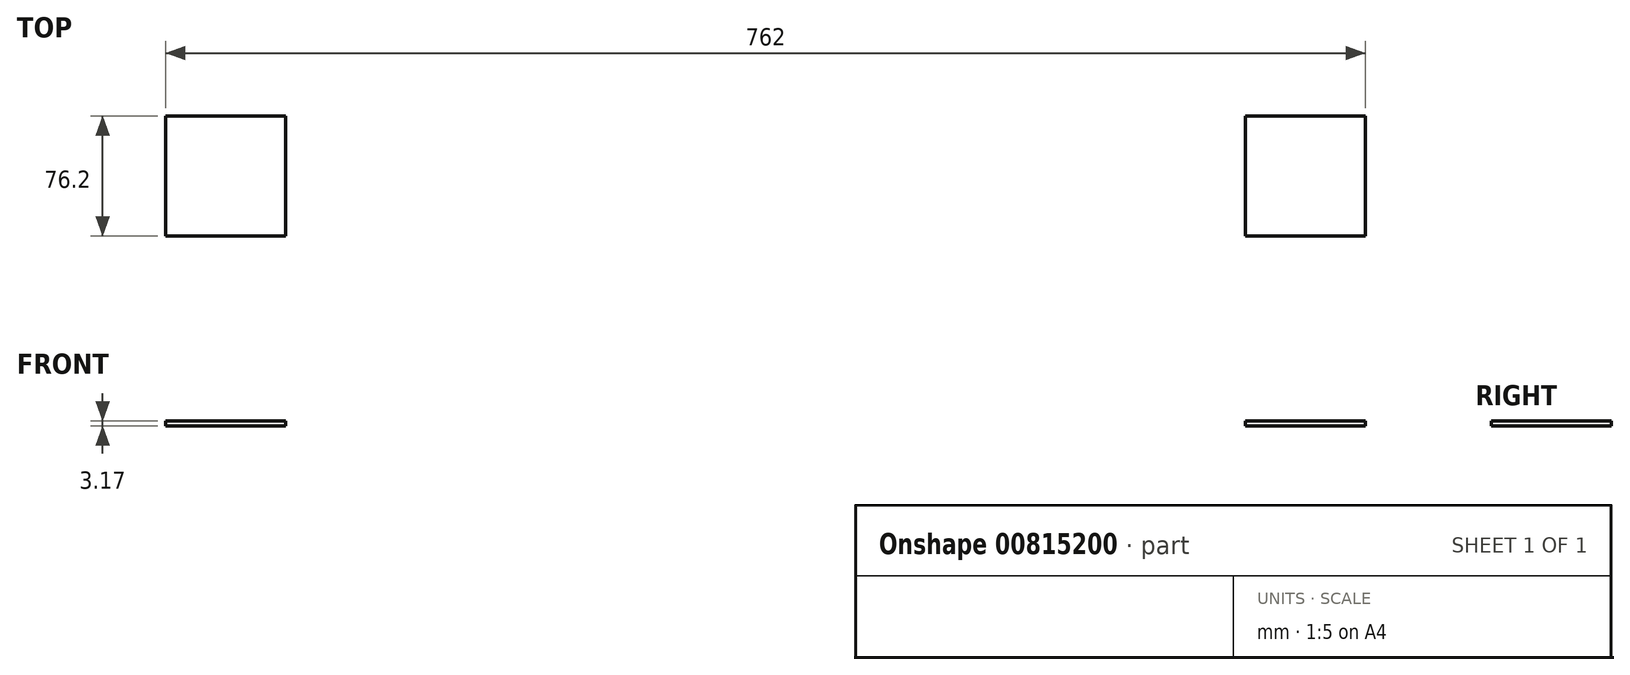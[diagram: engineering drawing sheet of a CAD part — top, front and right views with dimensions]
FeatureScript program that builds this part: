
annotation { "Feature Type Name" : "Feature", "Feature Type Description" : "" }
export const myFeature = defineFeature(function(context is Context, id is Id, definition is map)
    precondition{}
    {
        {
            var Q0;
            Q0=qCreatedBy(makeId("Top.planeOp"),FACE);
            var sketch = newSketch(context, id + "F0", { "sketchPlane" : qUnion([Q0])});
            skLineSegment(sketch, "E0.bottom", {"start": v(0, 0) * mm, "end": v(-762, 0) * mm});
            skLineSegment(sketch, "E0.top", {"start": v(0, -508) * mm, "end": v(-762, -508) * mm});
            skLineSegment(sketch, "E0.left", {"start": v(0, 0) * mm, "end": v(0, -508) * mm});
            skLineSegment(sketch, "E0.right", {"start": v(-762, 0) * mm, "end": v(-762, -508) * mm});
            skCircle(sketch, "E1", {"center": v(-101.6, -469.9) * mm, "radius": 12.7 * mm});
            skCircle(sketch, "E2.0.1.0", {"center": v(-101.6, -431.8) * mm, "radius": 12.7 * mm});
            skCircle(sketch, "E2.0.2.0", {"center": v(-101.6, -393.7) * mm, "radius": 12.7 * mm});
            skCircle(sketch, "E2.0.3.0", {"center": v(-101.6, -355.6) * mm, "radius": 12.7 * mm});
            skCircle(sketch, "E2.0.4.0", {"center": v(-101.6, -317.5) * mm, "radius": 12.7 * mm});
            skCircle(sketch, "E2.0.5.0", {"center": v(-101.6, -279.4) * mm, "radius": 12.7 * mm});
            skCircle(sketch, "E2.1.0.0", {"center": v(-139.7, -469.9) * mm, "radius": 12.7 * mm});
            skCircle(sketch, "E2.1.1.0", {"center": v(-139.7, -431.8) * mm, "radius": 12.7 * mm});
            skCircle(sketch, "E2.1.2.0", {"center": v(-139.7, -393.7) * mm, "radius": 12.7 * mm});
            skCircle(sketch, "E2.1.3.0", {"center": v(-139.7, -355.6) * mm, "radius": 12.7 * mm});
            skCircle(sketch, "E2.1.4.0", {"center": v(-139.7, -317.5) * mm, "radius": 12.7 * mm});
            skCircle(sketch, "E2.1.5.0", {"center": v(-139.7, -279.4) * mm, "radius": 12.7 * mm});
            skCircle(sketch, "E2.2.0.0", {"center": v(-177.8, -469.9) * mm, "radius": 12.7 * mm});
            skCircle(sketch, "E2.2.1.0", {"center": v(-177.8, -431.8) * mm, "radius": 12.7 * mm});
            skCircle(sketch, "E2.2.2.0", {"center": v(-177.8, -393.7) * mm, "radius": 12.7 * mm});
            skCircle(sketch, "E2.2.3.0", {"center": v(-177.8, -355.6) * mm, "radius": 12.7 * mm});
            skCircle(sketch, "E2.2.4.0", {"center": v(-177.8, -317.5) * mm, "radius": 12.7 * mm});
            skCircle(sketch, "E2.2.5.0", {"center": v(-177.8, -279.4) * mm, "radius": 12.7 * mm});
            skCircle(sketch, "E2.3.0.0", {"center": v(-215.9, -469.9) * mm, "radius": 12.7 * mm});
            skCircle(sketch, "E2.3.1.0", {"center": v(-215.9, -431.8) * mm, "radius": 12.7 * mm});
            skCircle(sketch, "E2.3.2.0", {"center": v(-215.9, -393.7) * mm, "radius": 12.7 * mm});
            skCircle(sketch, "E2.3.3.0", {"center": v(-215.9, -355.6) * mm, "radius": 12.7 * mm});
            skCircle(sketch, "E2.3.4.0", {"center": v(-215.9, -317.5) * mm, "radius": 12.7 * mm});
            skCircle(sketch, "E2.3.5.0", {"center": v(-215.9, -279.4) * mm, "radius": 12.7 * mm});
            skCircle(sketch, "E2.4.0.0", {"center": v(-254, -469.9) * mm, "radius": 12.7 * mm});
            skCircle(sketch, "E2.4.1.0", {"center": v(-254, -431.8) * mm, "radius": 12.7 * mm});
            skCircle(sketch, "E2.4.2.0", {"center": v(-254, -393.7) * mm, "radius": 12.7 * mm});
            skCircle(sketch, "E2.4.3.0", {"center": v(-254, -355.6) * mm, "radius": 12.7 * mm});
            skCircle(sketch, "E2.4.4.0", {"center": v(-254, -317.5) * mm, "radius": 12.7 * mm});
            skCircle(sketch, "E2.4.5.0", {"center": v(-254, -279.4) * mm, "radius": 12.7 * mm});
            skCircle(sketch, "E2.5.0.0", {"center": v(-292.1, -469.9) * mm, "radius": 12.7 * mm});
            skCircle(sketch, "E2.5.1.0", {"center": v(-292.1, -431.8) * mm, "radius": 12.7 * mm});
            skCircle(sketch, "E2.5.2.0", {"center": v(-292.1, -393.7) * mm, "radius": 12.7 * mm});
            skCircle(sketch, "E2.5.3.0", {"center": v(-292.1, -355.6) * mm, "radius": 12.7 * mm});
            skCircle(sketch, "E2.5.4.0", {"center": v(-292.1, -317.5) * mm, "radius": 12.7 * mm});
            skCircle(sketch, "E2.5.5.0", {"center": v(-292.1, -279.4) * mm, "radius": 12.7 * mm});
            skCircle(sketch, "E2.6.0.0", {"center": v(-330.2, -469.9) * mm, "radius": 12.7 * mm});
            skCircle(sketch, "E2.6.1.0", {"center": v(-330.2, -431.8) * mm, "radius": 12.7 * mm});
            skCircle(sketch, "E2.6.2.0", {"center": v(-330.2, -393.7) * mm, "radius": 12.7 * mm});
            skCircle(sketch, "E2.6.3.0", {"center": v(-330.2, -355.6) * mm, "radius": 12.7 * mm});
            skCircle(sketch, "E2.6.4.0", {"center": v(-330.2, -317.5) * mm, "radius": 12.7 * mm});
            skCircle(sketch, "E2.6.5.0", {"center": v(-330.2, -279.4) * mm, "radius": 12.7 * mm});
            skCircle(sketch, "E2.7.0.0", {"center": v(-368.3, -469.9) * mm, "radius": 12.7 * mm});
            skCircle(sketch, "E2.7.1.0", {"center": v(-368.3, -431.8) * mm, "radius": 12.7 * mm});
            skCircle(sketch, "E2.7.2.0", {"center": v(-368.3, -393.7) * mm, "radius": 12.7 * mm});
            skCircle(sketch, "E2.7.3.0", {"center": v(-368.3, -355.6) * mm, "radius": 12.7 * mm});
            skCircle(sketch, "E2.7.4.0", {"center": v(-368.3, -317.5) * mm, "radius": 12.7 * mm});
            skCircle(sketch, "E2.7.5.0", {"center": v(-368.3, -279.4) * mm, "radius": 12.7 * mm});
            skCircle(sketch, "E2.8.0.0", {"center": v(-406.4, -469.9) * mm, "radius": 12.7 * mm});
            skCircle(sketch, "E2.8.1.0", {"center": v(-406.4, -431.8) * mm, "radius": 12.7 * mm});
            skCircle(sketch, "E2.8.2.0", {"center": v(-406.4, -393.7) * mm, "radius": 12.7 * mm});
            skCircle(sketch, "E2.8.3.0", {"center": v(-406.4, -355.6) * mm, "radius": 12.7 * mm});
            skCircle(sketch, "E2.8.4.0", {"center": v(-406.4, -317.5) * mm, "radius": 12.7 * mm});
            skCircle(sketch, "E2.8.5.0", {"center": v(-406.4, -279.4) * mm, "radius": 12.7 * mm});
            skCircle(sketch, "E2.9.0.0", {"center": v(-444.5, -469.9) * mm, "radius": 12.7 * mm});
            skCircle(sketch, "E2.9.1.0", {"center": v(-444.5, -431.8) * mm, "radius": 12.7 * mm});
            skCircle(sketch, "E2.9.2.0", {"center": v(-444.5, -393.7) * mm, "radius": 12.7 * mm});
            skCircle(sketch, "E2.9.3.0", {"center": v(-444.5, -355.6) * mm, "radius": 12.7 * mm});
            skCircle(sketch, "E2.9.4.0", {"center": v(-444.5, -317.5) * mm, "radius": 12.7 * mm});
            skCircle(sketch, "E2.9.5.0", {"center": v(-444.5, -279.4) * mm, "radius": 12.7 * mm});
            skCircle(sketch, "E2.10.0.0", {"center": v(-482.6, -469.9) * mm, "radius": 12.7 * mm});
            skCircle(sketch, "E2.10.1.0", {"center": v(-482.6, -431.8) * mm, "radius": 12.7 * mm});
            skCircle(sketch, "E2.10.2.0", {"center": v(-482.6, -393.7) * mm, "radius": 12.7 * mm});
            skCircle(sketch, "E2.10.3.0", {"center": v(-482.6, -355.6) * mm, "radius": 12.7 * mm});
            skCircle(sketch, "E2.10.4.0", {"center": v(-482.6, -317.5) * mm, "radius": 12.7 * mm});
            skCircle(sketch, "E2.10.5.0", {"center": v(-482.6, -279.4) * mm, "radius": 12.7 * mm});
            skCircle(sketch, "E2.11.0.0", {"center": v(-520.7, -469.9) * mm, "radius": 12.7 * mm});
            skCircle(sketch, "E2.11.1.0", {"center": v(-520.7, -431.8) * mm, "radius": 12.7 * mm});
            skCircle(sketch, "E2.11.2.0", {"center": v(-520.7, -393.7) * mm, "radius": 12.7 * mm});
            skCircle(sketch, "E2.11.3.0", {"center": v(-520.7, -355.6) * mm, "radius": 12.7 * mm});
            skCircle(sketch, "E2.11.4.0", {"center": v(-520.7, -317.5) * mm, "radius": 12.7 * mm});
            skCircle(sketch, "E2.11.5.0", {"center": v(-520.7, -279.4) * mm, "radius": 12.7 * mm});
            skLineSegment(sketch, "E2.direction1", {"start": v(-101.6, -469.9) * mm, "end": v(-139.7, -469.9) * mm, "construction": true});
            skLineSegment(sketch, "E2.direction2", {"start": v(-101.6, -469.9) * mm, "end": v(-101.6, -431.8) * mm, "construction": true});
            skLineSegment(sketch, "E3.bottom", {"start": v(0, -508) * mm, "end": v(-76.2, -508) * mm});
            skLineSegment(sketch, "E3.top", {"start": v(0, -431.8) * mm, "end": v(-76.2, -431.8) * mm});
            skLineSegment(sketch, "E3.left", {"start": v(0, -508) * mm, "end": v(0, -431.8) * mm});
            skLineSegment(sketch, "E3.right", {"start": v(-76.2, -508) * mm, "end": v(-76.2, -431.8) * mm});
            skLineSegment(sketch, "E4.bottom", {"start": v(0, 0) * mm, "end": v(-76.2, 0) * mm});
            skLineSegment(sketch, "E4.top", {"start": v(0, -76.2) * mm, "end": v(-76.2, -76.2) * mm});
            skLineSegment(sketch, "E4.left", {"start": v(0, 0) * mm, "end": v(0, -76.2) * mm});
            skLineSegment(sketch, "E4.right", {"start": v(-76.2, 0) * mm, "end": v(-76.2, -76.2) * mm});
            skLineSegment(sketch, "E5.bottom", {"start": v(-762, -508) * mm, "end": v(-685.8, -508) * mm});
            skLineSegment(sketch, "E5.top", {"start": v(-762, -431.8) * mm, "end": v(-685.8, -431.8) * mm});
            skLineSegment(sketch, "E5.left", {"start": v(-762, -508) * mm, "end": v(-762, -431.8) * mm});
            skLineSegment(sketch, "E5.right", {"start": v(-685.8, -508) * mm, "end": v(-685.8, -431.8) * mm});
            skLineSegment(sketch, "E6.bottom", {"start": v(-762, 0) * mm, "end": v(-685.8, 0) * mm});
            skLineSegment(sketch, "E6.top", {"start": v(-762, -76.2) * mm, "end": v(-685.8, -76.2) * mm});
            skLineSegment(sketch, "E6.left", {"start": v(-762, 0) * mm, "end": v(-762, -76.2) * mm});
            skLineSegment(sketch, "E6.right", {"start": v(-685.8, 0) * mm, "end": v(-685.8, -76.2) * mm});
            skCircle(sketch, "E7.0.12.0", {"center": v(-558.8, -469.9) * mm, "radius": 12.7 * mm});
            skCircle(sketch, "E7.0.12.1", {"center": v(-558.8, -431.8) * mm, "radius": 12.7 * mm});
            skCircle(sketch, "E7.0.12.2", {"center": v(-558.8, -393.7) * mm, "radius": 12.7 * mm});
            skCircle(sketch, "E7.0.12.3", {"center": v(-558.8, -355.6) * mm, "radius": 12.7 * mm});
            skCircle(sketch, "E7.0.12.4", {"center": v(-558.8, -317.5) * mm, "radius": 12.7 * mm});
            skCircle(sketch, "E7.0.12.5", {"center": v(-558.8, -279.4) * mm, "radius": 12.7 * mm});
            skCircle(sketch, "E7.0.13.0", {"center": v(-596.9, -469.9) * mm, "radius": 12.7 * mm});
            skCircle(sketch, "E7.0.13.1", {"center": v(-596.9, -431.8) * mm, "radius": 12.7 * mm});
            skCircle(sketch, "E7.0.13.2", {"center": v(-596.9, -393.7) * mm, "radius": 12.7 * mm});
            skCircle(sketch, "E7.0.13.3", {"center": v(-596.9, -355.6) * mm, "radius": 12.7 * mm});
            skCircle(sketch, "E7.0.13.4", {"center": v(-596.9, -317.5) * mm, "radius": 12.7 * mm});
            skCircle(sketch, "E7.0.13.5", {"center": v(-596.9, -279.4) * mm, "radius": 12.7 * mm});
            skCircle(sketch, "E8.0.14.0", {"center": v(-635, -469.9) * mm, "radius": 12.7 * mm});
            skCircle(sketch, "E8.0.14.1", {"center": v(-635, -431.8) * mm, "radius": 12.7 * mm});
            skCircle(sketch, "E8.0.14.2", {"center": v(-635, -393.7) * mm, "radius": 12.7 * mm});
            skCircle(sketch, "E8.0.14.3", {"center": v(-635, -355.6) * mm, "radius": 12.7 * mm});
            skCircle(sketch, "E8.0.14.4", {"center": v(-635, -317.5) * mm, "radius": 12.7 * mm});
            skCircle(sketch, "E8.0.14.5", {"center": v(-635, -279.4) * mm, "radius": 12.7 * mm});
            skCircle(sketch, "E9.0.0.6", {"center": v(-101.6, -241.3) * mm, "radius": 12.7 * mm});
            skCircle(sketch, "E9.0.1.6", {"center": v(-139.7, -241.3) * mm, "radius": 12.7 * mm});
            skCircle(sketch, "E9.0.2.6", {"center": v(-177.8, -241.3) * mm, "radius": 12.7 * mm});
            skCircle(sketch, "E9.0.3.6", {"center": v(-215.9, -241.3) * mm, "radius": 12.7 * mm});
            skCircle(sketch, "E9.0.4.6", {"center": v(-254, -241.3) * mm, "radius": 12.7 * mm});
            skCircle(sketch, "E9.0.5.6", {"center": v(-292.1, -241.3) * mm, "radius": 12.7 * mm});
            skCircle(sketch, "E9.0.6.6", {"center": v(-330.2, -241.3) * mm, "radius": 12.7 * mm});
            skCircle(sketch, "E9.0.7.6", {"center": v(-368.3, -241.3) * mm, "radius": 12.7 * mm});
            skCircle(sketch, "E9.0.8.6", {"center": v(-406.4, -241.3) * mm, "radius": 12.7 * mm});
            skCircle(sketch, "E9.0.9.6", {"center": v(-444.5, -241.3) * mm, "radius": 12.7 * mm});
            skCircle(sketch, "E9.0.10.6", {"center": v(-482.6, -241.3) * mm, "radius": 12.7 * mm});
            skCircle(sketch, "E9.0.11.6", {"center": v(-520.7, -241.3) * mm, "radius": 12.7 * mm});
            skCircle(sketch, "E9.0.12.6", {"center": v(-558.8, -241.3) * mm, "radius": 12.7 * mm});
            skCircle(sketch, "E9.0.13.6", {"center": v(-596.9, -241.3) * mm, "radius": 12.7 * mm});
            skCircle(sketch, "E9.0.14.6", {"center": v(-635, -241.3) * mm, "radius": 12.7 * mm});
            skCircle(sketch, "E10.0.0.7", {"center": v(-101.6, -203.2) * mm, "radius": 12.7 * mm});
            skCircle(sketch, "E10.0.1.7", {"center": v(-139.7, -203.2) * mm, "radius": 12.7 * mm});
            skCircle(sketch, "E10.0.2.7", {"center": v(-177.8, -203.2) * mm, "radius": 12.7 * mm});
            skCircle(sketch, "E10.0.3.7", {"center": v(-215.9, -203.2) * mm, "radius": 12.7 * mm});
            skCircle(sketch, "E10.0.4.7", {"center": v(-254, -203.2) * mm, "radius": 12.7 * mm});
            skCircle(sketch, "E10.0.5.7", {"center": v(-292.1, -203.2) * mm, "radius": 12.7 * mm});
            skCircle(sketch, "E10.0.6.7", {"center": v(-330.2, -203.2) * mm, "radius": 12.7 * mm});
            skCircle(sketch, "E10.0.7.7", {"center": v(-368.3, -203.2) * mm, "radius": 12.7 * mm});
            skCircle(sketch, "E10.0.8.7", {"center": v(-406.4, -203.2) * mm, "radius": 12.7 * mm});
            skCircle(sketch, "E10.0.9.7", {"center": v(-444.5, -203.2) * mm, "radius": 12.7 * mm});
            skCircle(sketch, "E10.0.10.7", {"center": v(-482.6, -203.2) * mm, "radius": 12.7 * mm});
            skCircle(sketch, "E10.0.11.7", {"center": v(-520.7, -203.2) * mm, "radius": 12.7 * mm});
            skCircle(sketch, "E10.0.12.7", {"center": v(-558.8, -203.2) * mm, "radius": 12.7 * mm});
            skCircle(sketch, "E10.0.13.7", {"center": v(-596.9, -203.2) * mm, "radius": 12.7 * mm});
            skCircle(sketch, "E10.0.14.7", {"center": v(-635, -203.2) * mm, "radius": 12.7 * mm});
            skCircle(sketch, "E11.0.0.8", {"center": v(-101.6, -165.1) * mm, "radius": 12.7 * mm});
            skCircle(sketch, "E11.0.0.9", {"center": v(-101.6, -127) * mm, "radius": 12.7 * mm});
            skCircle(sketch, "E11.0.1.8", {"center": v(-139.7, -165.1) * mm, "radius": 12.7 * mm});
            skCircle(sketch, "E11.0.1.9", {"center": v(-139.7, -127) * mm, "radius": 12.7 * mm});
            skCircle(sketch, "E11.0.2.8", {"center": v(-177.8, -165.1) * mm, "radius": 12.7 * mm});
            skCircle(sketch, "E11.0.2.9", {"center": v(-177.8, -127) * mm, "radius": 12.7 * mm});
            skCircle(sketch, "E11.0.3.8", {"center": v(-215.9, -165.1) * mm, "radius": 12.7 * mm});
            skCircle(sketch, "E11.0.3.9", {"center": v(-215.9, -127) * mm, "radius": 12.7 * mm});
            skCircle(sketch, "E11.0.4.8", {"center": v(-254, -165.1) * mm, "radius": 12.7 * mm});
            skCircle(sketch, "E11.0.4.9", {"center": v(-254, -127) * mm, "radius": 12.7 * mm});
            skCircle(sketch, "E11.0.5.8", {"center": v(-292.1, -165.1) * mm, "radius": 12.7 * mm});
            skCircle(sketch, "E11.0.5.9", {"center": v(-292.1, -127) * mm, "radius": 12.7 * mm});
            skCircle(sketch, "E11.0.6.8", {"center": v(-330.2, -165.1) * mm, "radius": 12.7 * mm});
            skCircle(sketch, "E11.0.6.9", {"center": v(-330.2, -127) * mm, "radius": 12.7 * mm});
            skCircle(sketch, "E11.0.7.8", {"center": v(-368.3, -165.1) * mm, "radius": 12.7 * mm});
            skCircle(sketch, "E11.0.7.9", {"center": v(-368.3, -127) * mm, "radius": 12.7 * mm});
            skCircle(sketch, "E11.0.8.8", {"center": v(-406.4, -165.1) * mm, "radius": 12.7 * mm});
            skCircle(sketch, "E11.0.8.9", {"center": v(-406.4, -127) * mm, "radius": 12.7 * mm});
            skCircle(sketch, "E11.0.9.8", {"center": v(-444.5, -165.1) * mm, "radius": 12.7 * mm});
            skCircle(sketch, "E11.0.9.9", {"center": v(-444.5, -127) * mm, "radius": 12.7 * mm});
            skCircle(sketch, "E11.0.10.8", {"center": v(-482.6, -165.1) * mm, "radius": 12.7 * mm});
            skCircle(sketch, "E11.0.10.9", {"center": v(-482.6, -127) * mm, "radius": 12.7 * mm});
            skCircle(sketch, "E11.0.11.8", {"center": v(-520.7, -165.1) * mm, "radius": 12.7 * mm});
            skCircle(sketch, "E11.0.11.9", {"center": v(-520.7, -127) * mm, "radius": 12.7 * mm});
            skCircle(sketch, "E11.0.12.8", {"center": v(-558.8, -165.1) * mm, "radius": 12.7 * mm});
            skCircle(sketch, "E11.0.12.9", {"center": v(-558.8, -127) * mm, "radius": 12.7 * mm});
            skCircle(sketch, "E11.0.13.8", {"center": v(-596.9, -165.1) * mm, "radius": 12.7 * mm});
            skCircle(sketch, "E11.0.13.9", {"center": v(-596.9, -127) * mm, "radius": 12.7 * mm});
            skCircle(sketch, "E11.0.14.8", {"center": v(-635, -165.1) * mm, "radius": 12.7 * mm});
            skCircle(sketch, "E11.0.14.9", {"center": v(-635, -127) * mm, "radius": 12.7 * mm});
            skCircle(sketch, "E12.0.0.10", {"center": v(-101.6, -88.9) * mm, "radius": 12.7 * mm});
            skCircle(sketch, "E12.0.0.11", {"center": v(-101.6, -50.8) * mm, "radius": 12.7 * mm});
            skCircle(sketch, "E12.0.1.10", {"center": v(-139.7, -88.9) * mm, "radius": 12.7 * mm});
            skCircle(sketch, "E12.0.1.11", {"center": v(-139.7, -50.8) * mm, "radius": 12.7 * mm});
            skCircle(sketch, "E12.0.2.10", {"center": v(-177.8, -88.9) * mm, "radius": 12.7 * mm});
            skCircle(sketch, "E12.0.2.11", {"center": v(-177.8, -50.8) * mm, "radius": 12.7 * mm});
            skCircle(sketch, "E12.0.3.10", {"center": v(-215.9, -88.9) * mm, "radius": 12.7 * mm});
            skCircle(sketch, "E12.0.3.11", {"center": v(-215.9, -50.8) * mm, "radius": 12.7 * mm});
            skCircle(sketch, "E12.0.4.10", {"center": v(-254, -88.9) * mm, "radius": 12.7 * mm});
            skCircle(sketch, "E12.0.4.11", {"center": v(-254, -50.8) * mm, "radius": 12.7 * mm});
            skCircle(sketch, "E12.0.5.10", {"center": v(-292.1, -88.9) * mm, "radius": 12.7 * mm});
            skCircle(sketch, "E12.0.5.11", {"center": v(-292.1, -50.8) * mm, "radius": 12.7 * mm});
            skCircle(sketch, "E12.0.6.10", {"center": v(-330.2, -88.9) * mm, "radius": 12.7 * mm});
            skCircle(sketch, "E12.0.6.11", {"center": v(-330.2, -50.8) * mm, "radius": 12.7 * mm});
            skCircle(sketch, "E12.0.7.10", {"center": v(-368.3, -88.9) * mm, "radius": 12.7 * mm});
            skCircle(sketch, "E12.0.7.11", {"center": v(-368.3, -50.8) * mm, "radius": 12.7 * mm});
            skCircle(sketch, "E12.0.8.10", {"center": v(-406.4, -88.9) * mm, "radius": 12.7 * mm});
            skCircle(sketch, "E12.0.8.11", {"center": v(-406.4, -50.8) * mm, "radius": 12.7 * mm});
            skCircle(sketch, "E12.0.9.10", {"center": v(-444.5, -88.9) * mm, "radius": 12.7 * mm});
            skCircle(sketch, "E12.0.9.11", {"center": v(-444.5, -50.8) * mm, "radius": 12.7 * mm});
            skCircle(sketch, "E12.0.10.10", {"center": v(-482.6, -88.9) * mm, "radius": 12.7 * mm});
            skCircle(sketch, "E12.0.10.11", {"center": v(-482.6, -50.8) * mm, "radius": 12.7 * mm});
            skCircle(sketch, "E12.0.11.10", {"center": v(-520.7, -88.9) * mm, "radius": 12.7 * mm});
            skCircle(sketch, "E12.0.11.11", {"center": v(-520.7, -50.8) * mm, "radius": 12.7 * mm});
            skCircle(sketch, "E12.0.12.10", {"center": v(-558.8, -88.9) * mm, "radius": 12.7 * mm});
            skCircle(sketch, "E12.0.12.11", {"center": v(-558.8, -50.8) * mm, "radius": 12.7 * mm});
            skCircle(sketch, "E12.0.13.10", {"center": v(-596.9, -88.9) * mm, "radius": 12.7 * mm});
            skCircle(sketch, "E12.0.13.11", {"center": v(-596.9, -50.8) * mm, "radius": 12.7 * mm});
            skCircle(sketch, "E12.0.14.10", {"center": v(-635, -88.9) * mm, "radius": 12.7 * mm});
            skCircle(sketch, "E12.0.14.11", {"center": v(-635, -50.8) * mm, "radius": 12.7 * mm});
            skSolve(sketch);
        }
        {
            var Q0;
            {var subQ11=sQuery(id+"F0.wireOp",EDGE,"E0.bottom");Q0=makeQuery(id+"F0.imprint","IMPRINT",FACE,{"disambiguationData":[TD([[makeQuery(id+"F0.imprint","IMPRINT",EDGE,{"derivedFrom":subQ11}),1.0]])]});}
            var Q1;
            Q1=makeQuery(id+"F0.imprint","IMPRINT",FACE,{"disambiguationData":[TD([[makeQuery(id+"F0.imprint","IMPRINT",EDGE,{"derivedFrom":sQuery(id+"F0.wireOp",EDGE,"E2.14.0.0")}),-1.0]])]});
            extrude(context, id + "F1", {"entities" : qUnion([Q0, Q1]), "depth" : 3.17 * mm, "offsetDistance" : 25.4 * mm});
        }
    });
